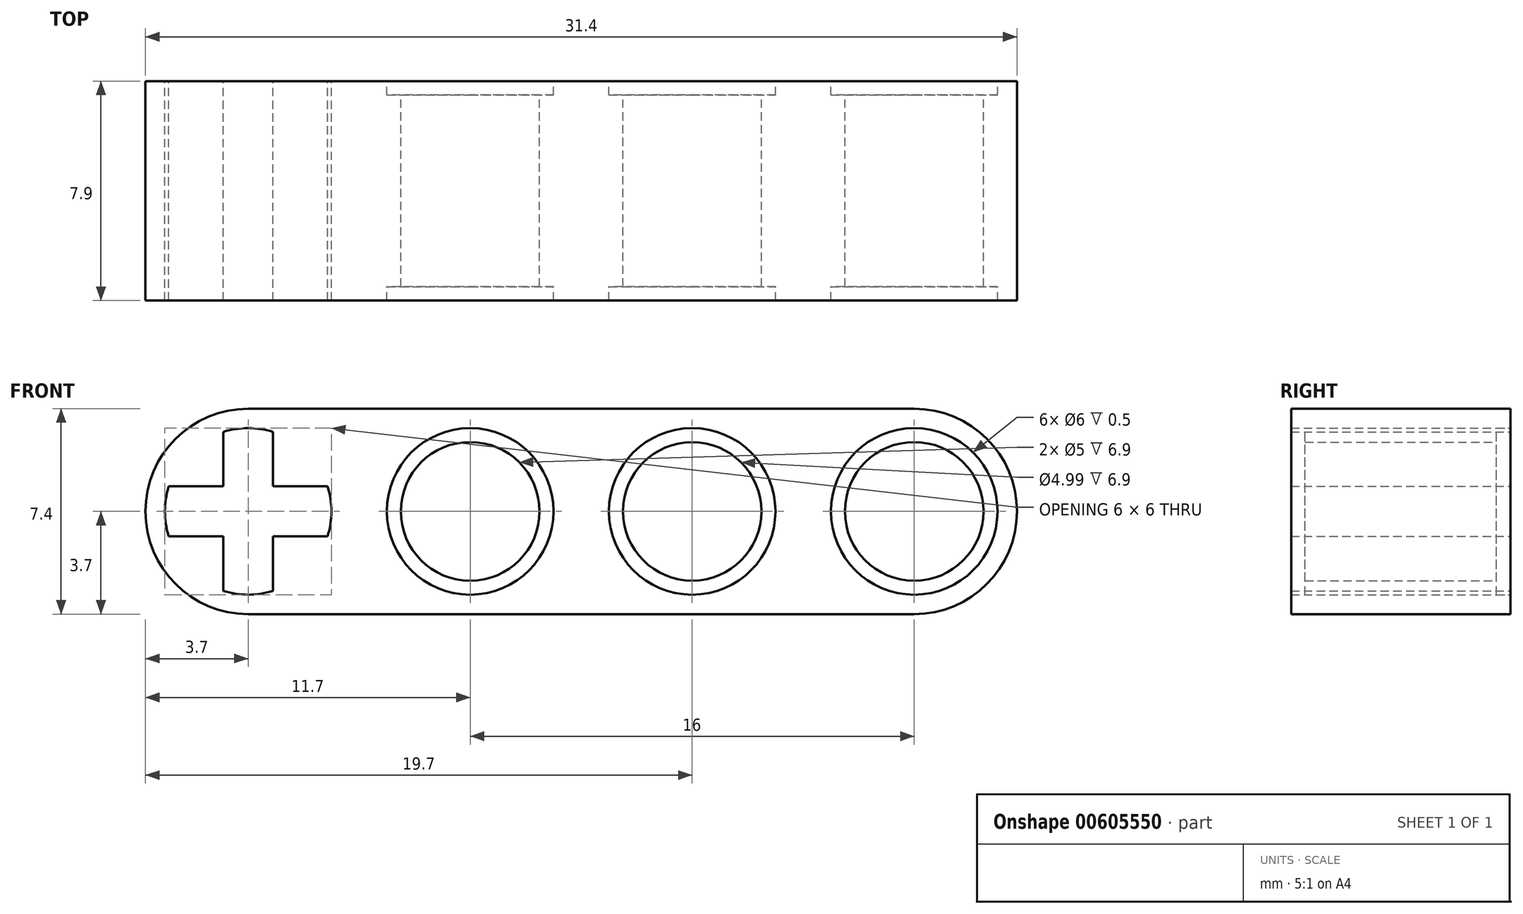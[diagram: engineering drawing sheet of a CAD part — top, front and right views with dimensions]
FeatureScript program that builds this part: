
annotation { "Feature Type Name" : "Feature", "Feature Type Description" : "" }
export const myFeature = defineFeature(function(context is Context, id is Id, definition is map)
    precondition{}
    {
        {
            var Q0;
            Q0=qCreatedBy(makeId("Front.planeOp"),FACE);
            var sketch = newSketch(context, id + "F0", { "sketchPlane" : qUnion([Q0])});
            skLineSegment(sketch, "E0", {"start": v(15.7, 0) * mm, "end": v(15.7, -3.7) * mm});
            skLineSegment(sketch, "E1", {"start": v(15.7, -3.7) * mm, "end": v(15.7, 3.7) * mm});
            skLineSegment(sketch, "E2", {"start": v(15.7, 3.7) * mm, "end": v(-15.7, 3.7) * mm});
            skLineSegment(sketch, "E3", {"start": v(-15.7, 3.7) * mm, "end": v(-15.7, -3.7) * mm});
            skLineSegment(sketch, "E4", {"start": v(-15.7, -3.7) * mm, "end": v(15.7, -3.7) * mm});
            skCircle(sketch, "E5", {"center": v(12, 0) * mm, "radius": 3 * mm});
            skCircle(sketch, "E6", {"center": v(4, 0) * mm, "radius": 3 * mm});
            skCircle(sketch, "E7", {"center": v(-4, 0) * mm, "radius": 3 * mm});
            skArc(sketch, "E8", {"start": v(-11.1, 2.86) * mm, "mid": v(-12, 3) * mm, "end": v(-12.9, 2.86) * mm});
            skLineSegment(sketch, "E9", {"start": v(-12.9, 0.9) * mm, "end": v(-14.86, 0.9) * mm});
            skLineSegment(sketch, "E10", {"start": v(-12.9, -0.9) * mm, "end": v(-14.86, -0.9) * mm});
            skLineSegment(sketch, "E11", {"start": v(-11.1, -0.9) * mm, "end": v(-9.14, -0.9) * mm});
            skLineSegment(sketch, "E12", {"start": v(-11.1, 0.9) * mm, "end": v(-9.14, 0.9) * mm});
            skLineSegment(sketch, "E13", {"start": v(-12.9, 0.9) * mm, "end": v(-12.9, 2.86) * mm});
            skLineSegment(sketch, "E14", {"start": v(-12.9, -0.9) * mm, "end": v(-12.9, -2.86) * mm});
            skLineSegment(sketch, "E15", {"start": v(-11.1, -0.9) * mm, "end": v(-11.1, -2.86) * mm});
            skLineSegment(sketch, "E16", {"start": v(-11.1, -2.86) * mm, "end": v(-11.1, -0.9) * mm});
            skArc(sketch, "E17.trimOffspring", {"start": v(-14.86, 0.9) * mm, "mid": v(-15, 0) * mm, "end": v(-14.86, -0.9) * mm});
            skArc(sketch, "E18.trimOffspring", {"start": v(-12.9, -2.86) * mm, "mid": v(-12, -3) * mm, "end": v(-11.1, -2.86) * mm});
            skArc(sketch, "E19.trimOffspring", {"start": v(-9.14, -0.9) * mm, "mid": v(-9, 0) * mm, "end": v(-9.14, 0.9) * mm});
            skLineSegment(sketch, "E20.trimOffspring", {"start": v(-11.1, 0.9) * mm, "end": v(-11.1, 2.86) * mm});
            skCircle(sketch, "E21", {"center": v(-4, 0) * mm, "radius": 2.5 * mm});
            skCircle(sketch, "E22", {"center": v(4, 0) * mm, "radius": 2.5 * mm});
            skCircle(sketch, "E23", {"center": v(12, 0) * mm, "radius": 2.5 * mm});
            skSolve(sketch);
        }
        {
            var Q0;
            {var subQ2=sQuery(id+"F0.wireOp",EDGE,"E2");Q0=makeQuery(id+"F0.imprint","IMPRINT",FACE,{"disambiguationData":[TD([[makeQuery(id+"F0.imprint","IMPRINT",EDGE,{"derivedFrom":subQ2}),1.0]])]});}
            extrude(context, id + "F1", {"entities" : qUnion([Q0]), "endBound" : BoundingType.SYMMETRIC, "depth" : 7.9 * mm, "offsetDistance" : 25 * mm});
        }
        {
            var Q0;
            Q0=makeQuery(id+"F0.imprint","IMPRINT",FACE,{"disambiguationData":[TD([[makeQuery(id+"F0.imprint","IMPRINT",EDGE,{"derivedFrom":sQuery(id+"F0.wireOp",EDGE,"E7")}),1.0]])]});
            var Q1;
            Q1=makeQuery(id+"F0.imprint","IMPRINT",FACE,{"disambiguationData":[TD([[makeQuery(id+"F0.imprint","IMPRINT",EDGE,{"derivedFrom":sQuery(id+"F0.wireOp",EDGE,"E6")}),1.0]])]});
            var Q2;
            Q2=makeQuery(id+"F0.imprint","IMPRINT",FACE,{"disambiguationData":[TD([[makeQuery(id+"F0.imprint","IMPRINT",EDGE,{"derivedFrom":sQuery(id+"F0.wireOp",EDGE,"E5")}),1.0]])]});
            extrude(context, id + "F2", {"entities" : qUnion([Q0, Q1, Q2]), "operationType" : NewBodyOperationType.ADD, "endBound" : BoundingType.SYMMETRIC, "depth" : 6.9 * mm, "offsetDistance" : 25 * mm});
        }
        {
            var Q0;
            Q0=makeQuery(id+"F1.opExtrude","SWEPT_EDGE",EDGE,{"disambiguationData":[OSD([sQuery(id+"F0.wireOp",EDGE,"E2"),sQuery(id+"F0.wireOp",EDGE,"E3")])]});
            var Q1;
            Q1=makeQuery(id+"F1.opExtrude","SWEPT_EDGE",EDGE,{"disambiguationData":[OSD([sQuery(id+"F0.wireOp",EDGE,"E3"),sQuery(id+"F0.wireOp",EDGE,"E4")])]});
            var Q2;
            Q2=makeQuery(id+"F1.opExtrude","SWEPT_EDGE",EDGE,{"disambiguationData":[OSD([sQuery(id+"F0.wireOp",EDGE,"E1"),sQuery(id+"F0.wireOp",EDGE,"E2")])]});
            var Q3;
            Q3=makeQuery(id+"F1.opExtrude","SWEPT_EDGE",EDGE,{"disambiguationData":[OSD([sQuery(id+"F0.wireOp",EDGE,"E1"),sQuery(id+"F0.wireOp",EDGE,"E4")])]});
            fillet(context, id + "F3", {"entities" : qUnion([Q0, Q1, Q2, Q3]), "radius" : 3.7 * mm, "tangentPropagation" : true, "allowEdgeOverflow" : false});
        }
    });
